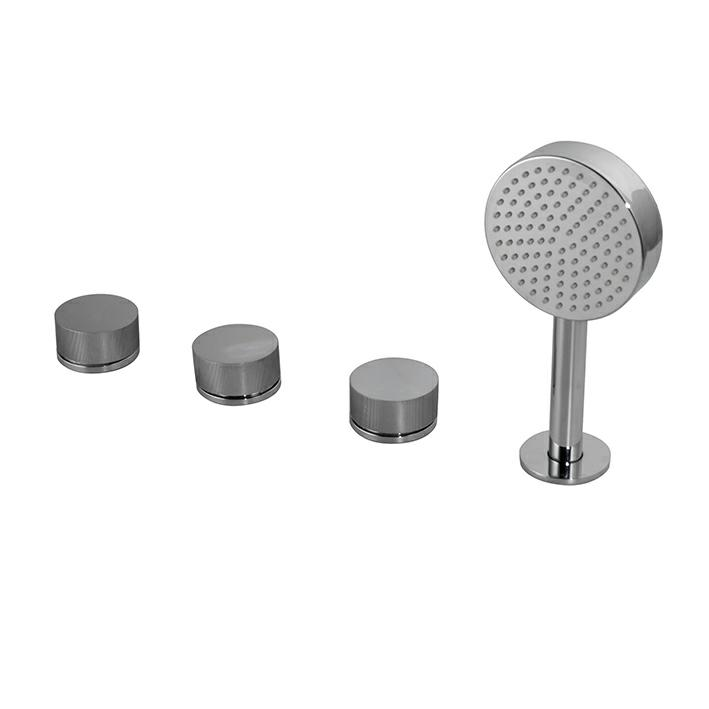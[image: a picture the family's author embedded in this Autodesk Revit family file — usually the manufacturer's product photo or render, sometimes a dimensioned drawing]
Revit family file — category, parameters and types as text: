
# Revit family: PGR_Noken_WtrSplyFitngsForBths_Tono
name_source: partatom
category: Plumbing Fixtures
revit_build: Autodesk Revit 2017 (Build: 20190508_0315(x64)
units: mm (PartAtom-declared; Revit-internal decimal feet)

## family parameters
Always vertical = Yes
Cut with Voids When Loaded = No
Host = Wall
OmniClass Number = 23.45.55.17
OmniClass Title = Mixing Faucets
Part Type = Normal
Room Calculation Point = No
Round Connector Dimension = Use Diameter
Shared = No

## types (1)
- Tono-100190247
    AccessibilityPerformance = See ProductInformation for technical PDF
    ApplicationType = Bath
    AssetType = Fixed
    BIMObjectName = PGR_Noken_WaterSupplyFittingsForBaths_Tono_Chrome-50x150x314 mm-100190247
    BodyMaterial = Brass
    Category = Pr_40_20_87_09: Bath taps
    CloseOffRating = 0.0 Pa
    CodePerformance = EN 817, EN 248, En 274
    Collection = Tono
    Color = Chrome
    Description = Deck mounted bathtub mixer 1/2”. Without pop-up waste. Flow rate 16 l/min and 15 l/min hand shower. at 3 bar. Material brass, finish chrome plated. 5 years warranty for superficial finishes and 2 years for the rest of components. EN 817, EN 248
    DurationUnit = year
    FaucetFunction = Mixed
    FaucetOperation = LeverHandle
    FaucetTopDescription = Lever
    FaucetType = Pillar
    Features = See ProductInformation for technical PDF
    Finish = Chrome
    FlowCoefficient = 0
    FlowPressure = 0.0
    Height = 1500 mm  [stored 4.92126 ft]
    IfcExportAs = IfcValveType
    IfcExportType = Faucet
    InletConnectionSize = 0 mm  [stored 0 ft]
    ManufacturerURL = www.noken.com
    Material = Brass
    MaterialMetal = PGR_Noken_Brass_Chrome
    MaterialPlastic = PGR_Noken_Plastic_Gray
    Model = 100190247
    ModelNumber = 100190247
    ModelReference = BATERIA INSTAL. BAÑERA TONO 4 PIEZAS CR
    NBSDescription = Water supply fittings for baths
    NBSReference = 45-35-70/315
    Name = WaterSupplyFittingsForBaths_Tono_Chrome-50x150x314 mm-100190247
    NettWeight = 0
    NominalHeight = 55 mm  [stored 0.180446 ft]
    NominalLength = 480 mm  [stored 1.5748 ft]
    NominalWidth = 205 mm  [stored 0.672572 ft]
    NumberOfConnections = 0
    OutletConnectionSize = 0 mm  [stored 0 ft]
    ProductInformation = http://calidad.info-grupo.com:8081
    Reference = -
    Size = 50x150x314 mm
    Status = Unset
    SustainabilityPerformance = See ProductInformation for technical PDF
    TechnicalDrawing = See ProductInformation for technical PDF
    TestPressure = 0.0 Pa
    Type Image = 100190247.jpg
    URL = www.noken.com
    Uniclass2015Code = Pr_40_20_87_09
    Uniclass2015Title = Bath taps
    Uniclass2015Version = V1_9
    ValveMechanism = Unset
    ValveOperation = Lever
    ValvePattern = Unset
    Version = 1
    WarrantyDescription = See ProductInformation for technical PDF
    WarrantyDurationUnit = year

note: source unit labels omitted for FlowPressure — the stored unit's dimension contradicts the parameter name (converter mislabeling)

note: [stored X ft] marks values corroborated as IEEE doubles in the binary element streams (Revit-internal decimal feet)

## geometry (parser evidence)
native form markers: Blend x2, Sweep x5
no freeform markers — native parametric forms only
